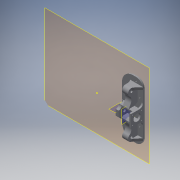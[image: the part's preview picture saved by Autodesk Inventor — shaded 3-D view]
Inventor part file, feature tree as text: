
AUTODESK INVENTOR PART (.ipt)
format: ipt  version: 2016 (Build 200138000, 138)  size: 446,464 bytes
history: native  units: in
note: dims shown in document units (in); Inventor stores cm internally (conversion verified against a paired STEP export)
features: sketch x14, extrude x12, projected_geometry x8, fillet x6, plane x3, chamfer x2, reference x1
ambient origin geometry x8: Origin, YZ Plane, XZ Plane, XY Plane, X Axis, Y Axis, Z Axis, Center Point
bodies: Solid1 (feature_tree)
feature tree (46):
  plane  "Work Plane1"
  extrude  "Extrusion1"  Depth=0.2in TaperAngle=0.0deg
  extrude  "Extrusion2"  TaperAngle=90.0deg  [1 undecoded]
  extrude  "Extrusion3"  Depth=1.7in
  extrude  "Extrusion4"  Depth=0.6102in
  extrude  "Extrusion5"  Depth=0.1181in
  extrude  "Extrusion6"  Depth=0.2362in TaperAngle=0.0deg
  extrude  "Extrusion7"  Depth=0.8in
  plane  "Work Plane2"
  extrude  "Extrusion8"  Depth=1.4961in TaperAngle=0.0deg
  extrude  "Extrusion9"  Depth=0.3937in TaperAngle=0.0deg
  fillet  "Fillet1"  Radius=0.45in
  fillet  "Fillet2"  Radius=0.45in
  fillet  "Fillet3"  Radius=0.45in
  sketch  "Sketch10"  dims[d33=0.45in d34=0.8312in d35=0.0in]
  sketch  "Sketch11"  dims[d36=0.3937in d37=0.0787in d38=0.0in]
  chamfer  "Chamfer1"  Distance=0.8312in
  chamfer  "Chamfer2"  Distance=0.0787in
  extrude  "Extrusion10"  Depth=0.9375in
  extrude  "Extrusion11"  Depth=2.7559in
  plane  "Work Plane3"
  extrude  "Extrusion12"  Depth=0.5in
  fillet  "Fillet4"  Radius=0.315in
  fillet  "Fillet5"  Radius=1.0in
  fillet  "Fillet6"  Radius=1.0in
  sketch  "Sketch1"  dims[d0=8.0in d1=0.2in d2=0.0in]
  reference  "Reference1"
  sketch  "Sketch2"  dims[d3=0.85in d4=90.0deg]
  projected_geometry  "Projected Loop1"
  sketch  "Sketch3"  dims[d5=1.7in d6=1.7in]
  projected_geometry  "Projected Loop2"
  sketch  "Sketch4"  dims[d7=0.9843in d8=0.6102in]
  projected_geometry  "Projected Loop3"
  sketch  "Sketch5"  dims[d9=0.6102in d10=0.1181in]
  projected_geometry  "Projected Loop4"
  sketch  "Sketch6"  dims[d11=0.7874in d13=1.2205in d14=0.7874in d16=1.2205in d19=0.2362in d20=0.0in]
  projected_geometry  "Projected Loop5"
  sketch  "Sketch7"  dims[d21=0.8in d22=0.8in]
  projected_geometry  "Projected Loop6"
  sketch  "Sketch8"  dims[d23=0.8in d24=1.4961in d25=0.0in]
  sketch  "Sketch9"  dims[d26=0.8661in d27=0.3937in d28=0.0in d30=0.45in d31=0.45in d32=0.45in]
  sketch  "Sketch12"  dims[d39=0.4537in d40=0.0in d41=0.9375in]
  projected_geometry  "Projected Loop7"
  sketch  "Sketch13"  dims[d42=0.8287in d43=0.0in d45=2.7559in]
  projected_geometry  "Projected Loop8"
  sketch  "Sketch14"  dims[d46=0.315in d47=2.7559in d48=0.315in d49=1.0in d50=1.0in d51=0.8287in d52=0.0in d53=1.5625in d54=1.0in d55=0.8125in d56=0.1875in d57=0.125in d58=45.0deg d59=0.25in d60=0.125in d61=45.0deg d62=0.3287in d63=0.0in d64=0.3287in d65=0.0in d66=0.6412in d67=0.0in d68=0.8125in d69=0.8125in d70=0.5in]
note: 1 required parameter value undecoded (feature->parameter linkage not recoverable at this tier; creation-order binding heuristic only, values carry confidence <= 0.55)
